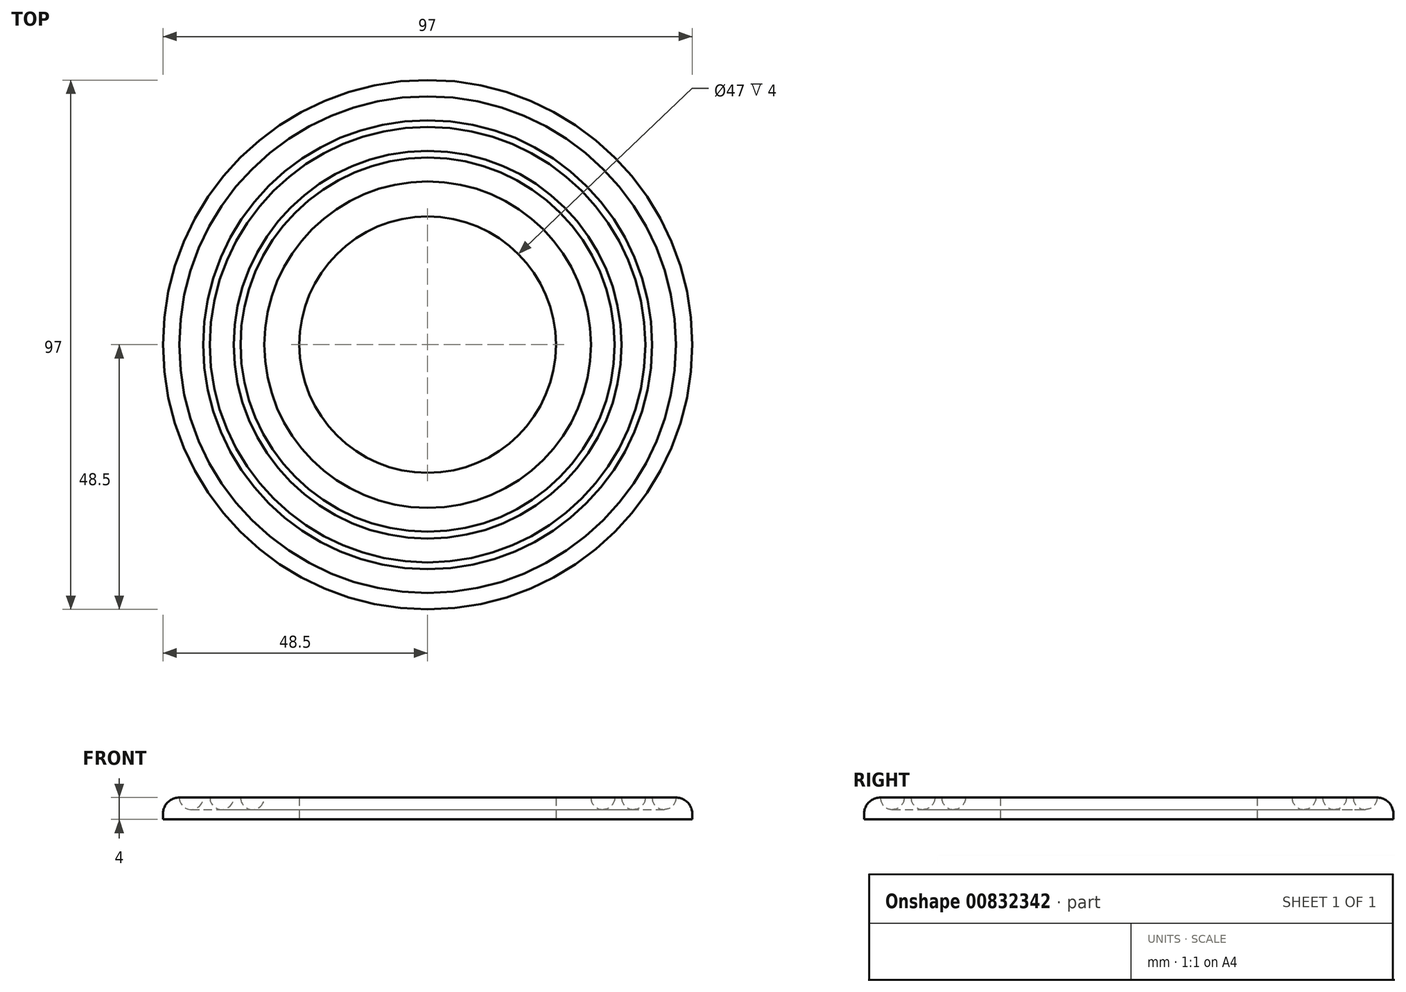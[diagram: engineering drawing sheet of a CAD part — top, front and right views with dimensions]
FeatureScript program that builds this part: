
annotation { "Feature Type Name" : "Feature", "Feature Type Description" : "" }
export const myFeature = defineFeature(function(context is Context, id is Id, definition is map)
    precondition{}
    {
        {
            var Q0;
            Q0=qCreatedBy(makeId("Front.planeOp"),FACE);
            var sketch = newSketch(context, id + "F0", { "sketchPlane" : qUnion([Q0])});
            skLineSegment(sketch, "E0", {"start": v(0, 0) * mm, "end": v(0, 3.83) * mm});
            skPoint(sketch, "E1.start.orphan", {"position": v(-4.84, 2) * mm});
            skPoint(sketch, "E2.start.orphan", {"position": v(-4.84, 0) * mm});
            skLineSegment(sketch, "E3", {"start": v(-23.5, 0) * mm, "end": v(-48.5, 0) * mm});
            skLineSegment(sketch, "E4", {"start": v(-48.5, 0) * mm, "end": v(-48.5, 1) * mm});
            skLineSegment(sketch, "E5", {"start": v(-41.13, 4) * mm, "end": v(-39.9, 4) * mm});
            skLineSegment(sketch, "E6", {"start": v(-23.5, 4) * mm, "end": v(-23.5, 0) * mm});
            skPoint(sketch, "E7.visualSharp", {"position": v(-48.5, 4) * mm});
            skArc(sketch, "E7.filletArc", {"start": v(-45.5, 4) * mm, "mid": v(-47.62, 3.12) * mm, "end": v(-48.5, 1) * mm});
            skArc(sketch, "E8", {"start": v(-45.5, 4) * mm, "mid": v(-43.32, 1.82) * mm, "end": v(-41.13, 4) * mm});
            skArc(sketch, "E9", {"start": v(-39.9, 4) * mm, "mid": v(-37.7, 1.82) * mm, "end": v(-35.52, 4) * mm});
            skLineSegment(sketch, "E10.trimOffspring", {"start": v(-35.52, 4) * mm, "end": v(-34.28, 4) * mm});
            skArc(sketch, "E11", {"start": v(-34.28, 4) * mm, "mid": v(-32.1, 1.82) * mm, "end": v(-29.91, 4) * mm});
            skLineSegment(sketch, "E12.trimOffspring", {"start": v(-29.91, 4) * mm, "end": v(-23.5, 4) * mm});
            skSolve(sketch);
        }
        {
            var Q0;
            Q0=makeQuery(id+"F0.imprint","IMPRINT",FACE,{"disambiguationData":[TD([[makeQuery(id+"F0.imprint","IMPRINT",EDGE,{"derivedFrom":sQuery(id+"F0.wireOp",EDGE,"E3")}),-1.0]])]});
            var Q1;
            Q1=sQuery(id+"F0.wireOp",EDGE,"E0");
            revolve(context, id + "F1", {"surfaceOperationType" : NewSurfaceOperationType.NEW, "entities" : qUnion([Q0]), "axis" : qUnion([Q1]), "revolveType" : RevolveType.FULL});
        }
    });
